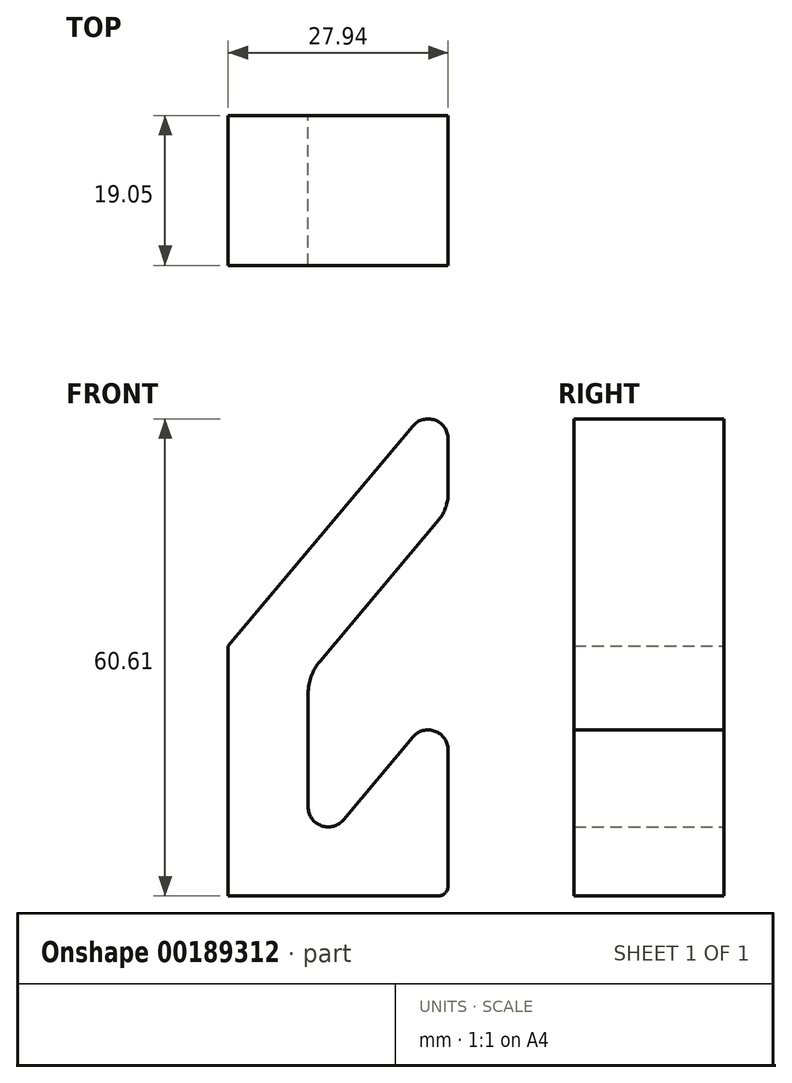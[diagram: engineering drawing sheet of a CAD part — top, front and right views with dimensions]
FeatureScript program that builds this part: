
annotation { "Feature Type Name" : "Feature", "Feature Type Description" : "" }
export const myFeature = defineFeature(function(context is Context, id is Id, definition is map)
    precondition{}
    {
        {
            var Q0;
            Q0=qCreatedBy(makeId("Front.planeOp"),FACE);
            var sketch = newSketch(context, id + "F0", { "sketchPlane" : qUnion([Q0])});
            skLineSegment(sketch, "E0.bottom", {"start": v(0, 0) * mm, "end": v(26.67, 0) * mm});
            skLineSegment(sketch, "E0.left", {"start": v(0, 0) * mm, "end": v(0, 31.75) * mm});
            skLineSegment(sketch, "E0.right", {"start": v(27.94, 1.27) * mm, "end": v(27.94, 18.55) * mm});
            skLineSegment(sketch, "E1", {"start": v(26.75, 47.83) * mm, "end": v(11.65, 29.82) * mm});
            skLineSegment(sketch, "E2", {"start": v(10.16, 25.74) * mm, "end": v(10.16, 11.32) * mm});
            skLineSegment(sketch, "E3", {"start": v(14.65, 9.69) * mm, "end": v(23.45, 20.19) * mm});
            skPoint(sketch, "E4.visualSharp", {"position": v(27.94, 25.53) * mm});
            skArc(sketch, "E4.filletArc", {"start": v(27.94, 18.55) * mm, "mid": v(26.27, 20.94) * mm, "end": v(23.45, 20.19) * mm});
            skPoint(sketch, "E5.visualSharp", {"position": v(10.16, 28.05) * mm});
            skArc(sketch, "E6.filletArc", {"start": v(11.65, 29.82) * mm, "mid": v(10.54, 27.91) * mm, "end": v(10.16, 25.74) * mm});
            skPoint(sketch, "E7.visualSharp", {"position": v(10.16, 4.34) * mm});
            skArc(sketch, "E7.filletArc", {"start": v(10.16, 11.32) * mm, "mid": v(11.83, 8.93) * mm, "end": v(14.65, 9.69) * mm});
            skPoint(sketch, "E8.visualSharp", {"position": v(27.94, 0) * mm});
            skArc(sketch, "E8.filletArc", {"start": v(26.67, 0) * mm, "mid": v(27.57, 0.37) * mm, "end": v(27.94, 1.27) * mm});
            skLineSegment(sketch, "E9", {"start": v(23.45, 59.7) * mm, "end": v(0, 31.75) * mm});
            skLineSegment(sketch, "E10", {"start": v(27.94, 58.07) * mm, "end": v(27.94, 51.1) * mm});
            skPoint(sketch, "E11.visualSharp", {"position": v(27.94, 65.05) * mm});
            skArc(sketch, "E11.filletArc", {"start": v(27.94, 58.07) * mm, "mid": v(26.27, 60.46) * mm, "end": v(23.45, 59.7) * mm});
            skPoint(sketch, "E12.visualSharp", {"position": v(27.94, 49.24) * mm});
            skArc(sketch, "E12.filletArc", {"start": v(26.75, 47.83) * mm, "mid": v(27.63, 49.35) * mm, "end": v(27.94, 51.1) * mm});
            skSolve(sketch);
        }
        {
            var Q0;
            Q0 = qSketchRegion(id + "F0", true);
            extrude(context, id + "F1", {"entities" : qUnion([Q0]), "depth" : 19.05 * mm});
        }
    });
